# Revit family: 15764chn_
name_source: partatom
category: Plumbing Fixtures
revit_build: Autodesk Revit 2018 (Build: 20170223_1515(x64)
units: mm (PartAtom-declared; Revit-internal decimal feet)

## family parameters
Always vertical = No
Cut with Voids When Loaded = No
OmniClass Number = 23.45.00.00
OmniClass Title = Sanitary, Laundry, and Cleaning Equipment
Part Type = Normal
Room Calculation Point = No
Round Connector Dimension = Use Diameter
Shared = No
Work Plane-Based = Yes

## types (5) — shared parameters
Always visible = Yes
BIMobject category = Showers
Default Elevation = 1219.2 mm  [stored 4 ft]
Design country = Germany
EAN code = 4059625209288
Edition number = 1
IFC Classification = Sanitary Terminal
Installation instructions = https://www.hansgrohe.com
Manufacturer country = Germany
Manufacturer name = hansgrohe
Product Guid = 3dd61a28-c323-4c15-b219-91a1a6d51c0c
Product SKU = 15764CHN
Product data url = https://www.bimobject.com
Product family = ShowerSelect
Product group = Shower thermostat
Product name = 15764CHN ShowerSelect Valve for concealed installation for 3 functions
Product url = https://www.hansgrohe.com
QR code = https://www.bimobject.com
Technical description = https://www.hansgrohe.com

## per-type parameters (varying)
| type | Material 1 |
| 340 Brushed Black Chrome | Hansgrohe - Pulsify - 340 Brushed Black Chrome |
| 140 Brushed Bronze | Hansgrohe - Pulsify - 140 Brushed Bronze |
| 670 Matte Black | Hansgrohe - Pulsify - 670 Matte Black |
| 700 Matt White | Hansgrohe - Pulsify - 700 Matt White |
| 990 Polished Gold Optic | Hansgrohe - Pulsify - 990 Polished Gold Optic |

note: [stored X ft] marks values corroborated as IEEE doubles in the binary element streams (Revit-internal decimal feet)

## geometry (parser evidence)
native form markers: Sweep x2
no freeform markers — native parametric forms only
